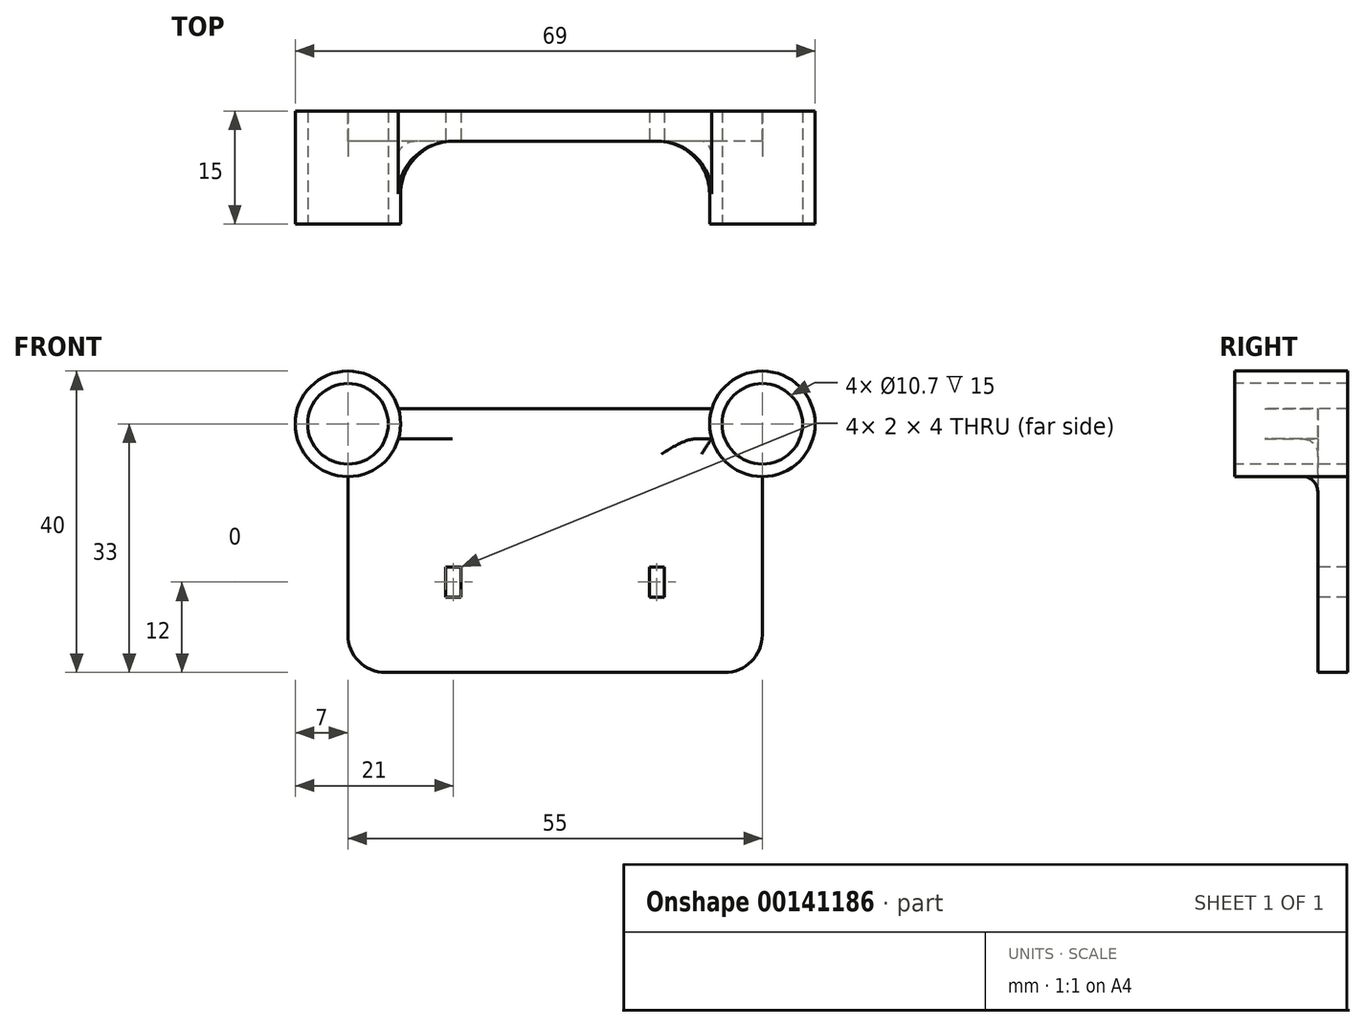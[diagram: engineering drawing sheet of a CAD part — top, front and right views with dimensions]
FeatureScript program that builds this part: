
annotation { "Feature Type Name" : "Feature", "Feature Type Description" : "" }
export const myFeature = defineFeature(function(context is Context, id is Id, definition is map)
    precondition{}
    {
        {
            var Q0;
            Q0=qCreatedBy(makeId("Front.planeOp"),FACE);
            cPlane(context, id + "F0", {"entities" : qUnion([Q0]), "cplaneType" : CPlaneType.OFFSET, "offset" : 0 * mm, "width" : 150 * mm, "height" : 150 * mm});
        }
        {
            var Q0;
            Q0=qCreatedBy(id+"F0.planeOp",FACE);
            var sketch = newSketch(context, id + "F1", { "sketchPlane" : qUnion([Q0])});
            skCircle(sketch, "E0", {"center": v(-27.5, 0) * mm, "radius": 7 * mm});
            skSolve(sketch);
        }
        {
            var Q0;
            Q0=qCreatedBy(id+"F0.planeOp",FACE);
            var sketch = newSketch(context, id + "F2", { "sketchPlane" : qUnion([Q0])});
            skCircle(sketch, "E1", {"center": v(27.5, 0) * mm, "radius": 7 * mm});
            skSolve(sketch);
        }
        {
            var Q0;
            Q0 = qSketchRegion(id + "F1", true);
            var Q1;
            Q1 = qSketchRegion(id + "F2", true);
            extrude(context, id + "F3", {"entities" : qUnion([Q0, Q1]), "oppositeDirection" : true, "depth" : 15 * mm});
        }
        {
            var Q0;
            Q0=qCreatedBy(id+"F0.planeOp",FACE);
            var sketch = newSketch(context, id + "F4", { "sketchPlane" : qUnion([Q0])});
            skCircle(sketch, "E2", {"center": v(-27.5, 0) * mm, "radius": 5.35 * mm});
            skSolve(sketch);
        }
        {
            var Q0;
            Q0=qCreatedBy(id+"F0.planeOp",FACE);
            var sketch = newSketch(context, id + "F5", { "sketchPlane" : qUnion([Q0])});
            skCircle(sketch, "E3", {"center": v(27.5, 0) * mm, "radius": 5.35 * mm});
            skSolve(sketch);
        }
        {
            var Q0;
            Q0 = qSketchRegion(id + "F4", true);
            var Q1;
            Q1 = qSketchRegion(id + "F5", true);
            extrude(context, id + "F6", {"entities" : qUnion([Q0, Q1]), "oppositeDirection" : true, "depth" : 30 * mm});
        }
        {
            var Q0;
            Q0=qCreatedBy(makeId("Right.planeOp"),FACE);
            var sketch = newSketch(context, id + "F7", { "sketchPlane" : qUnion([Q0])});
            skLineSegment(sketch, "E4.bottom", {"start": v(11, 2) * mm, "end": v(15, 2) * mm});
            skLineSegment(sketch, "E4.top", {"start": v(11, -2) * mm, "end": v(15, -2) * mm});
            skLineSegment(sketch, "E4.left", {"start": v(11, 2) * mm, "end": v(11, -2) * mm});
            skLineSegment(sketch, "E4.right", {"start": v(15, 2) * mm, "end": v(15, -2) * mm});
            skSolve(sketch);
        }
        {
            var Q0;
            Q0 = qSketchRegion(id + "F7", true);
            extrude(context, id + "F8", {"entities" : qUnion([Q0]), "endBound" : BoundingType.SYMMETRIC, "depth" : 50 * mm});
        }
        {
            var Q0;
            Q0=makeQuery(id+"F3.opExtrude","SWEPT_BODY",BODY,{"disambiguationData":[OSD([sQuery(id+"F1.wireOp",EDGE,"E0")])]});
            var Q1;
            Q1=makeQuery(id+"F3.opExtrude","SWEPT_BODY",BODY,{"disambiguationData":[OSD([sQuery(id+"F2.wireOp",EDGE,"E1")])]});
            var Q2;
            Q2=makeQuery(id+"F8.opExtrude","SWEPT_BODY",BODY,{"disambiguationData":[OSD([sQuery(id+"F7.wireOp",EDGE,"E4.bottom"),sQuery(id+"F7.wireOp",EDGE,"E4.top"),sQuery(id+"F7.wireOp",EDGE,"E4.left"),sQuery(id+"F7.wireOp",EDGE,"E4.right")])]});
            booleanBodies(context, id + "F9", {"operationType" : BooleanOperationType.UNION, "tools" : qUnion([Q0, Q1, Q2])});
        }
        {
            var Q0;
            Q0=makeQuery(id+"F9.opBoolean","INTERSECT",EDGE,{"derivedFrom":[makeQuery(id+"F3.opExtrude","SWEPT_FACE",FACE,{"disambiguationData":[OSD([sQuery(id+"F1.wireOp",EDGE,"E0")])]}),makeQuery(id+"F8.opExtrude","SWEPT_FACE",FACE,{"disambiguationData":[OSD([sQuery(id+"F7.wireOp",EDGE,"E4.left")])]})]});
            var Q1;
            Q1=makeQuery(id+"F9.opBoolean","INTERSECT",EDGE,{"derivedFrom":[makeQuery(id+"F3.opExtrude","SWEPT_FACE",FACE,{"disambiguationData":[OSD([sQuery(id+"F2.wireOp",EDGE,"E1")])]}),makeQuery(id+"F8.opExtrude","SWEPT_FACE",FACE,{"disambiguationData":[OSD([sQuery(id+"F7.wireOp",EDGE,"E4.left")])]})]});
            var Q2;
            Q2=makeQuery(id+"F9.opBoolean","INTERSECT",EDGE,{"derivedFrom":[makeQuery(id+"F3.opExtrude","SWEPT_FACE",FACE,{"disambiguationData":[OSD([sQuery(id+"F2.wireOp",EDGE,"E1")])]}),makeQuery(id+"F8.opExtrude","SWEPT_FACE",FACE,{"disambiguationData":[OSD([sQuery(id+"F7.wireOp",EDGE,"E4.right")])]})]});
            var Q3;
            Q3=makeQuery(id+"F9.opBoolean","INTERSECT",EDGE,{"derivedFrom":[makeQuery(id+"F3.opExtrude","SWEPT_FACE",FACE,{"disambiguationData":[OSD([sQuery(id+"F1.wireOp",EDGE,"E0")])]}),makeQuery(id+"F8.opExtrude","SWEPT_FACE",FACE,{"disambiguationData":[OSD([sQuery(id+"F7.wireOp",EDGE,"E4.right")])]})]});
            fillet(context, id + "F10", {"entities" : qUnion([Q0, Q1, Q2, Q3]), "radius" : 7 * mm, "tangentPropagation" : true, "allowEdgeOverflow" : false});
        }
        {
            var Q0;
            Q0=qCreatedBy(makeId("Right.planeOp"),FACE);
            var sketch = newSketch(context, id + "F11", { "sketchPlane" : qUnion([Q0])});
            skLineSegment(sketch, "E5.bottom", {"start": v(11, -2) * mm, "end": v(15, -2) * mm});
            skLineSegment(sketch, "E5.top", {"start": v(11, -33) * mm, "end": v(15, -33) * mm});
            skLineSegment(sketch, "E5.left", {"start": v(11, -2) * mm, "end": v(11, -33) * mm});
            skLineSegment(sketch, "E5.right", {"start": v(15, -2) * mm, "end": v(15, -33) * mm});
            skSolve(sketch);
        }
        {
            var Q0;
            Q0=makeQuery(id+"F11.imprint","IMPRINT",FACE,{"disambiguationData":[TD([[makeQuery(id+"F11.imprint","IMPRINT",EDGE,{"derivedFrom":sQuery(id+"F11.wireOp",EDGE,"E5.bottom")}),-1.0]])]});
            extrude(context, id + "F12", {"entities" : qUnion([Q0]), "endBound" : BoundingType.SYMMETRIC, "depth" : 55 * mm});
        }
        {
            var Q0;
            Q0=makeQuery(id+"F3.opExtrude","SWEPT_BODY",BODY,{"disambiguationData":[OSD([sQuery(id+"F1.wireOp",EDGE,"E0")])]});
            var Q1;
            Q1=makeQuery(id+"F12.opExtrude","SWEPT_BODY",BODY,{"disambiguationData":[OSD([sQuery(id+"F11.wireOp",EDGE,"E5.bottom"),sQuery(id+"F11.wireOp",EDGE,"E5.top"),sQuery(id+"F11.wireOp",EDGE,"E5.left"),sQuery(id+"F11.wireOp",EDGE,"E5.right")])]});
            booleanBodies(context, id + "F13", {"operationType" : BooleanOperationType.UNION, "tools" : qUnion([Q0, Q1])});
        }
        {
            var Q0;
            Q0=makeQuery(id+"F13.opBoolean","INTERSECT",EDGE,{"derivedFrom":[makeQuery(id+"F3.opExtrude","SWEPT_FACE",FACE,{"disambiguationData":[OSD([sQuery(id+"F1.wireOp",EDGE,"E0")])]}),makeQuery(id+"F12.opExtrude","SWEPT_FACE",FACE,{"disambiguationData":[OSD([sQuery(id+"F11.wireOp",EDGE,"E5.right")])]})]});
            var Q1;
            {var subQ1=sQuery(id+"F1.wireOp",EDGE,"E0");var subQ2=sQuery(id+"F11.wireOp",EDGE,"E5.right");Q1=makeQuery(id+"F13.opBoolean","SPLIT",EDGE,{"disambiguationData":[TD([makeQuery(id+"F3.opExtrude","SWEPT_FACE",FACE,{"disambiguationData":[OSD([subQ1])]})])],"derivedFrom":makeQuery(id+"F12.opExtrude","SWEPT_EDGE",EDGE,{"disambiguationData":[OSD([sQuery(id+"F11.wireOp",EDGE,"E5.bottom"),subQ2])]})});}
            var Q2;
            {var subQ1=sQuery(id+"F2.wireOp",EDGE,"E1");var subQ2=sQuery(id+"F11.wireOp",EDGE,"E5.right");Q2=makeQuery(id+"F13.opBoolean","SPLIT",EDGE,{"disambiguationData":[TD([makeQuery(id+"F3.opExtrude","SWEPT_FACE",FACE,{"disambiguationData":[OSD([subQ1])]})])],"derivedFrom":makeQuery(id+"F12.opExtrude","SWEPT_EDGE",EDGE,{"disambiguationData":[OSD([sQuery(id+"F11.wireOp",EDGE,"E5.bottom"),subQ2])]})});}
            var Q3;
            Q3=makeQuery(id+"F13.opBoolean","INTERSECT",EDGE,{"derivedFrom":[makeQuery(id+"F3.opExtrude","SWEPT_FACE",FACE,{"disambiguationData":[OSD([sQuery(id+"F2.wireOp",EDGE,"E1")])]}),makeQuery(id+"F12.opExtrude","SWEPT_FACE",FACE,{"disambiguationData":[OSD([sQuery(id+"F11.wireOp",EDGE,"E5.right")])]})]});
            var Q4;
            {var subQ1=sQuery(id+"F2.wireOp",EDGE,"E1");var subQ2=sQuery(id+"F11.wireOp",EDGE,"E5.left");Q4=makeQuery(id+"F13.opBoolean","SPLIT",EDGE,{"disambiguationData":[TD([makeQuery(id+"F3.opExtrude","SWEPT_FACE",FACE,{"disambiguationData":[OSD([subQ1])]})])],"derivedFrom":makeQuery(id+"F12.opExtrude","SWEPT_EDGE",EDGE,{"disambiguationData":[OSD([sQuery(id+"F11.wireOp",EDGE,"E5.bottom"),subQ2])]})});}
            var Q5;
            Q5=makeQuery(id+"F13.opBoolean","INTERSECT",EDGE,{"derivedFrom":[makeQuery(id+"F3.opExtrude","SWEPT_FACE",FACE,{"disambiguationData":[OSD([sQuery(id+"F2.wireOp",EDGE,"E1")])]}),makeQuery(id+"F12.opExtrude","SWEPT_FACE",FACE,{"disambiguationData":[OSD([sQuery(id+"F11.wireOp",EDGE,"E5.left")])]})]});
            var Q6;
            {var subQ1=sQuery(id+"F1.wireOp",EDGE,"E0");var subQ2=sQuery(id+"F11.wireOp",EDGE,"E5.left");Q6=makeQuery(id+"F13.opBoolean","SPLIT",EDGE,{"disambiguationData":[TD([makeQuery(id+"F3.opExtrude","SWEPT_FACE",FACE,{"disambiguationData":[OSD([subQ1])]})])],"derivedFrom":makeQuery(id+"F12.opExtrude","SWEPT_EDGE",EDGE,{"disambiguationData":[OSD([sQuery(id+"F11.wireOp",EDGE,"E5.bottom"),subQ2])]})});}
            var Q7;
            Q7=makeQuery(id+"F13.opBoolean","INTERSECT",EDGE,{"derivedFrom":[makeQuery(id+"F3.opExtrude","SWEPT_FACE",FACE,{"disambiguationData":[OSD([sQuery(id+"F1.wireOp",EDGE,"E0")])]}),makeQuery(id+"F12.opExtrude","SWEPT_FACE",FACE,{"disambiguationData":[OSD([sQuery(id+"F11.wireOp",EDGE,"E5.left")])]})]});
            fillet(context, id + "F14", {"entities" : qUnion([Q0, Q1, Q2, Q3, Q4, Q5, Q6, Q7]), "radius" : 2 * mm, "tangentPropagation" : true, "allowEdgeOverflow" : false});
        }
        {
            var Q0;
            Q0=makeQuery(id+"F12.opExtrude","CAP_EDGE",EDGE,{"disambiguationData":[OSD([sQuery(id+"F11.wireOp",EDGE,"E5.top")])],"isStart":false});
            var Q1;
            Q1=makeQuery(id+"F12.opExtrude","CAP_EDGE",EDGE,{"disambiguationData":[OSD([sQuery(id+"F11.wireOp",EDGE,"E5.top")])],"isStart":true});
            fillet(context, id + "F15", {"entities" : qUnion([Q0, Q1]), "radius" : 5 * mm, "tangentPropagation" : true, "allowEdgeOverflow" : false});
        }
        {
            var Q0;
            Q0=makeQuery(id+"F6.opExtrude","SWEPT_BODY",BODY,{"disambiguationData":[OSD([sQuery(id+"F4.wireOp",EDGE,"E2")])]});
            var Q1;
            Q1=makeQuery(id+"F6.opExtrude","SWEPT_BODY",BODY,{"disambiguationData":[OSD([sQuery(id+"F5.wireOp",EDGE,"E3")])]});
            var Q2;
            Q2=makeQuery(id+"F3.opExtrude","SWEPT_BODY",BODY,{"disambiguationData":[OSD([sQuery(id+"F1.wireOp",EDGE,"E0")])]});
            booleanBodies(context, id + "F16", {"operationType" : BooleanOperationType.SUBTRACTION, "tools" : qUnion([Q0, Q1]), "targets" : qUnion([Q2])});
        }
        {
            var Q0;
            Q0=makeQuery(id+"F13.opBoolean","MERGE",FACE,{"derivedFrom":[makeQuery(id+"F8.opExtrude","SWEPT_FACE",FACE,{"disambiguationData":[OSD([sQuery(id+"F7.wireOp",EDGE,"E4.left")])]}),makeQuery(id+"F12.opExtrude","SWEPT_FACE",FACE,{"disambiguationData":[OSD([sQuery(id+"F11.wireOp",EDGE,"E5.left")])]})]});
            var sketch = newSketch(context, id + "F17", { "sketchPlane" : qUnion([Q0])});
            skLineSegment(sketch, "E6.bottom", {"start": v(12.5, -19) * mm, "end": v(14.5, -19) * mm});
            skLineSegment(sketch, "E6.top", {"start": v(12.5, -23) * mm, "end": v(14.5, -23) * mm});
            skLineSegment(sketch, "E6.left", {"start": v(12.5, -19) * mm, "end": v(12.5, -23) * mm});
            skLineSegment(sketch, "E6.right", {"start": v(14.5, -19) * mm, "end": v(14.5, -23) * mm});
            skSolve(sketch);
        }
        {
            var Q0;
            Q0=makeQuery(id+"F17.imprint","IMPRINT",FACE,{"disambiguationData":[TD([[makeQuery(id+"F17.imprint","IMPRINT",EDGE,{"derivedFrom":sQuery(id+"F17.wireOp",EDGE,"E6.bottom")}),1.0]])]});
            var sketch = newSketch(context, id + "F18", { "sketchPlane" : qUnion([Q0])});
            skLineSegment(sketch, "E7.bottom", {"start": v(-14.5, -19) * mm, "end": v(-12.5, -19) * mm});
            skLineSegment(sketch, "E7.top", {"start": v(-14.5, -23) * mm, "end": v(-12.5, -23) * mm});
            skLineSegment(sketch, "E7.left", {"start": v(-14.5, -19) * mm, "end": v(-14.5, -23) * mm});
            skLineSegment(sketch, "E7.right", {"start": v(-12.5, -19) * mm, "end": v(-12.5, -23) * mm});
            skSolve(sketch);
        }
        {
            var Q0;
            Q0 = qSketchRegion(id + "F17", true);
            var Q1;
            Q1 = qSketchRegion(id + "F18", true);
            extrude(context, id + "F19", {"entities" : qUnion([Q0, Q1]), "oppositeDirection" : true, "depth" : 25 * mm});
        }
        {
            var Q0;
            Q0=makeQuery(id+"F19.opExtrude","SWEPT_BODY",BODY,{"disambiguationData":[OSD([sQuery(id+"F17.wireOp",EDGE,"E6.bottom"),sQuery(id+"F17.wireOp",EDGE,"E6.top"),sQuery(id+"F17.wireOp",EDGE,"E6.left"),sQuery(id+"F17.wireOp",EDGE,"E6.right")])]});
            var Q1;
            Q1=makeQuery(id+"F19.opExtrude","SWEPT_BODY",BODY,{"disambiguationData":[OSD([sQuery(id+"F18.wireOp",EDGE,"E7.bottom"),sQuery(id+"F18.wireOp",EDGE,"E7.top"),sQuery(id+"F18.wireOp",EDGE,"E7.left"),sQuery(id+"F18.wireOp",EDGE,"E7.right")])]});
            var Q2;
            Q2=makeQuery(id+"F3.opExtrude","SWEPT_BODY",BODY,{"disambiguationData":[OSD([sQuery(id+"F1.wireOp",EDGE,"E0")])]});
            booleanBodies(context, id + "F20", {"operationType" : BooleanOperationType.SUBTRACTION, "tools" : qUnion([Q0, Q1]), "targets" : qUnion([Q2])});
        }
    });
